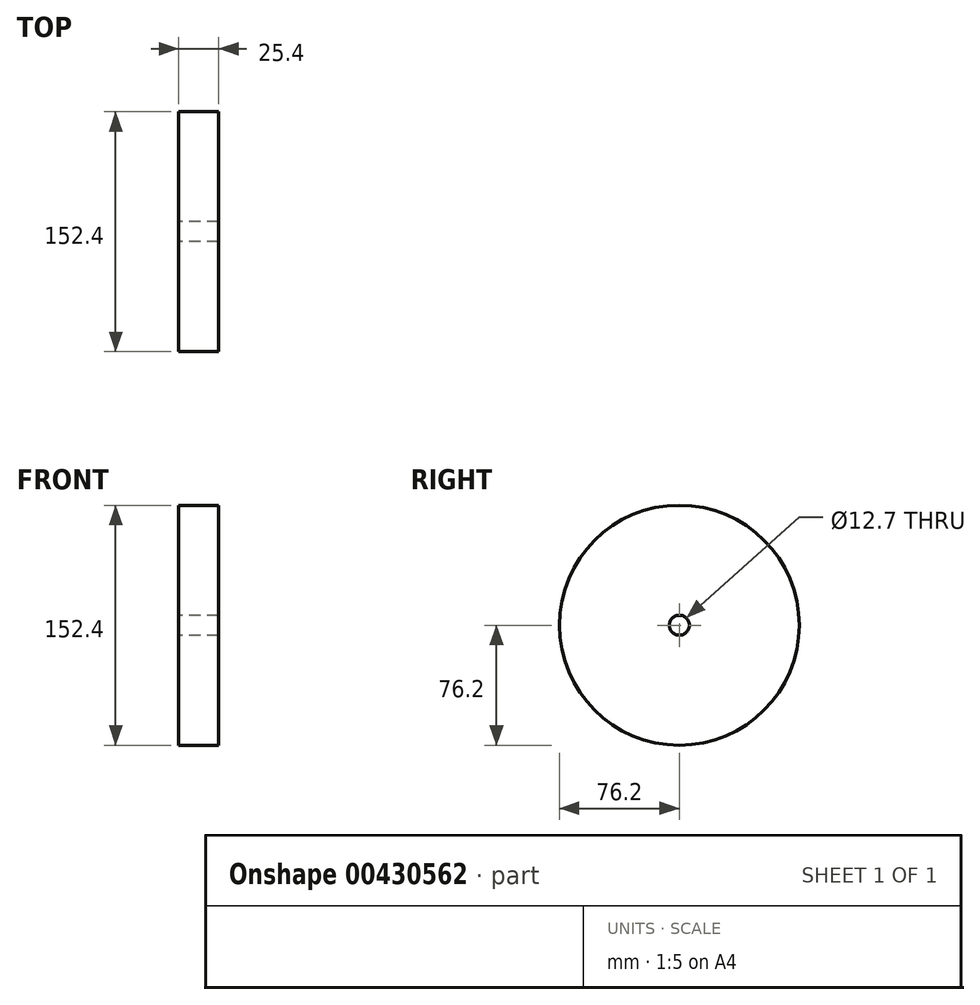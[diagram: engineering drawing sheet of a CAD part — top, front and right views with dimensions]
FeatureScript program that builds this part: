
annotation { "Feature Type Name" : "Feature", "Feature Type Description" : "" }
export const myFeature = defineFeature(function(context is Context, id is Id, definition is map)
    precondition{}
    {
        {
            var Q0;
            Q0=qCreatedBy(makeId("Right.planeOp"),FACE);
            var sketch = newSketch(context, id + "F0", { "sketchPlane" : qUnion([Q0])});
            skCircle(sketch, "E0", {"center": v(0, 0) * mm, "radius": 76.2 * mm});
            skCircle(sketch, "E1", {"center": v(0, 0) * mm, "radius": 6.35 * mm});
            skSolve(sketch);
        }
        {
            var Q0;
            Q0=makeQuery(id+"F0.imprint","IMPRINT",FACE,{"disambiguationData":[TD([[makeQuery(id+"F0.imprint","IMPRINT",EDGE,{"derivedFrom":sQuery(id+"F0.wireOp",EDGE,"E0")}),1.0]])]});
            extrude(context, id + "F1", {"entities" : qUnion([Q0]), "depth" : 25.4 * mm});
        }
    });
